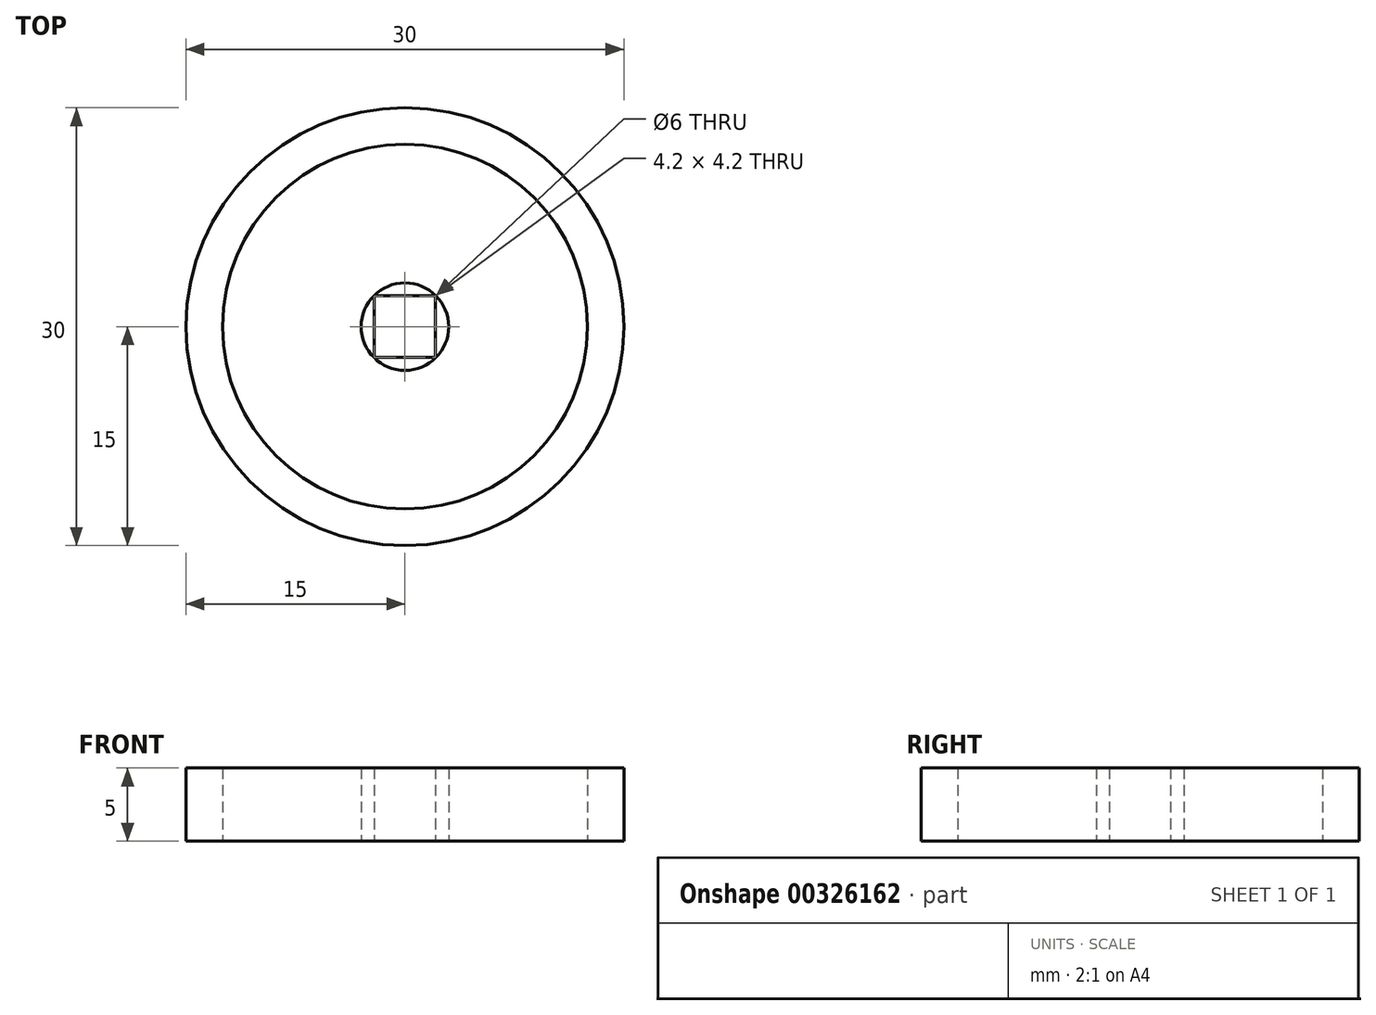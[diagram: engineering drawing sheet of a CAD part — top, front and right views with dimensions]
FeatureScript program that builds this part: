
annotation { "Feature Type Name" : "Feature", "Feature Type Description" : "" }
export const myFeature = defineFeature(function(context is Context, id is Id, definition is map)
    precondition{}
    {
        {
            var Q0;
            Q0=qCreatedBy(makeId("Top.planeOp"),FACE);
            var sketch = newSketch(context, id + "F0", { "sketchPlane" : qUnion([Q0])});
            skCircle(sketch, "E0", {"center": v(0, 0) * mm, "radius": 15 * mm});
            skLineSegment(sketch, "E1.bottom", {"start": v(2.1, 2.1) * mm, "end": v(-2.1, 2.1) * mm});
            skLineSegment(sketch, "E1.top", {"start": v(2.1, -2.1) * mm, "end": v(-2.1, -2.1) * mm});
            skLineSegment(sketch, "E1.left", {"start": v(2.1, 2.1) * mm, "end": v(2.1, -2.1) * mm});
            skLineSegment(sketch, "E1.right", {"start": v(-2.1, 2.1) * mm, "end": v(-2.1, -2.1) * mm});
            skSolve(sketch);
        }
        {
            var Q0;
            Q0 = qSketchRegion(id + "F0", true);
            extrude(context, id + "F1", {"entities" : qUnion([Q0]), "depth" : 5 * mm});
        }
        {
            var Q0;
            Q0=qCreatedBy(makeId("Top.planeOp"),FACE);
            var sketch = newSketch(context, id + "F2", { "sketchPlane" : qUnion([Q0])});
            skCircle(sketch, "E2", {"center": v(0, 0) * mm, "radius": 12.5 * mm});
            skCircle(sketch, "E3", {"center": v(0, 0) * mm, "radius": 3 * mm});
            skSolve(sketch);
        }
        {
            var Q0;
            Q0 = qSketchRegion(id + "F2", true);
            extrude(context, id + "F3", {"entities" : qUnion([Q0]), "depth" : 5 * mm});
        }
    });
